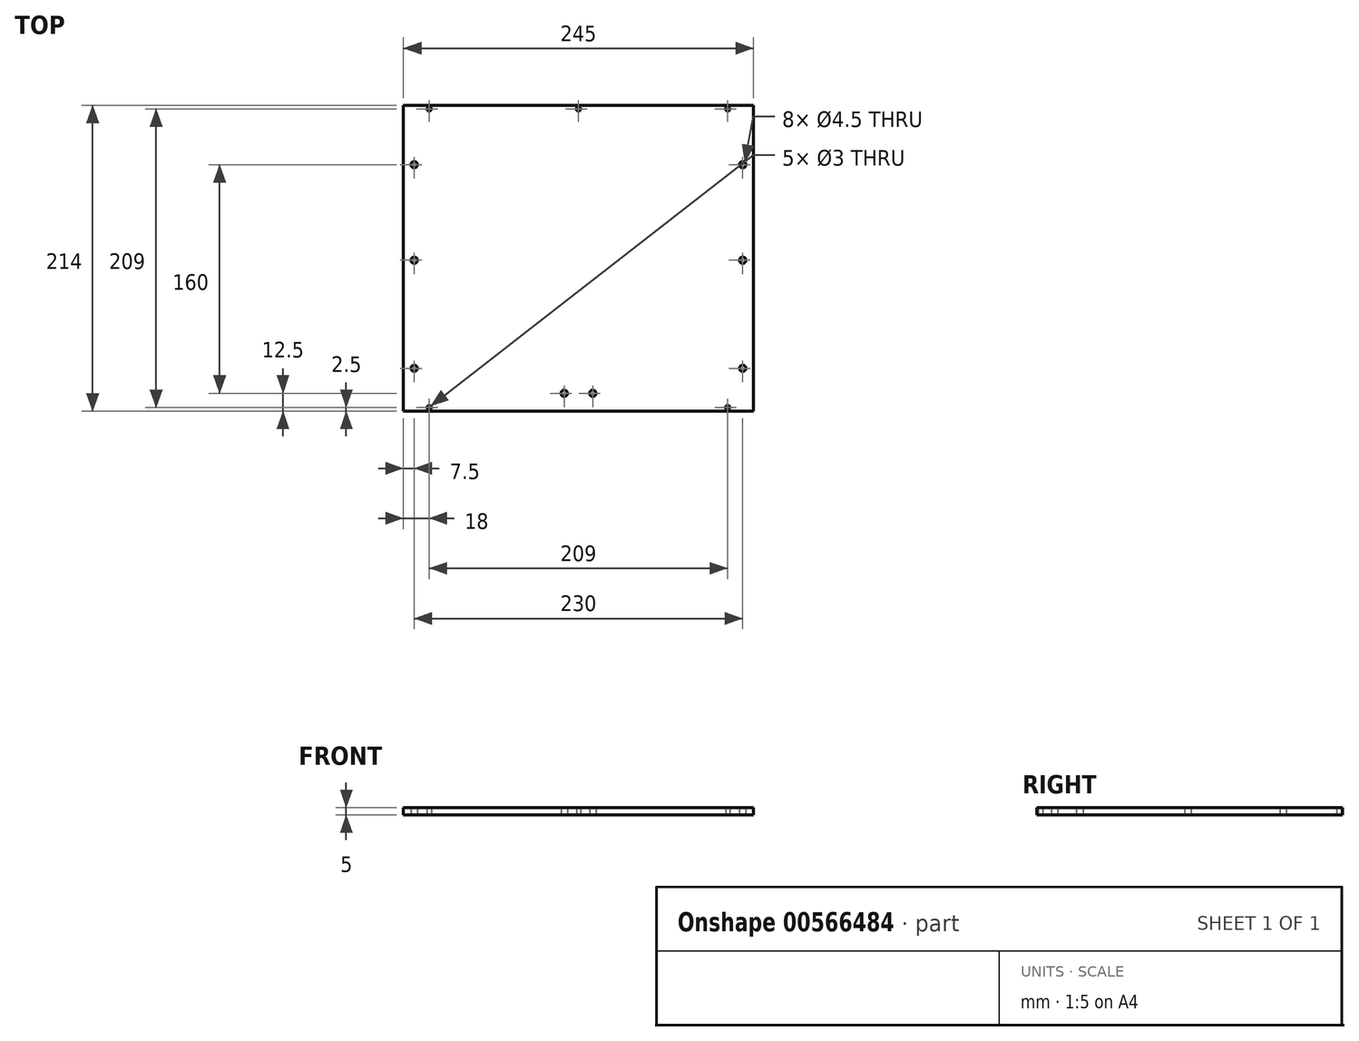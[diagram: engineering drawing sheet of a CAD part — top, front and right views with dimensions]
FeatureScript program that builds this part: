
annotation { "Feature Type Name" : "Feature", "Feature Type Description" : "" }
export const myFeature = defineFeature(function(context is Context, id is Id, definition is map)
    precondition{}
    {
        {
            var Q0;
            Q0=qCreatedBy(makeId("Top.planeOp"),FACE);
            var sketch = newSketch(context, id + "F0", { "sketchPlane" : qUnion([Q0])});
            skLineSegment(sketch, "E0.bottom", {"start": v(122.5, -107) * mm, "end": v(-122.5, -107) * mm});
            skLineSegment(sketch, "E0.top", {"start": v(122.5, 107) * mm, "end": v(-122.5, 107) * mm});
            skLineSegment(sketch, "E0.left", {"start": v(122.5, -107) * mm, "end": v(122.5, 0.95) * mm});
            skLineSegment(sketch, "E0.right", {"start": v(-122.5, -107) * mm, "end": v(-122.5, 0.95) * mm});
            skPoint(sketch, "E1.visualSharp", {"position": v(-122.5, 107) * mm});
            skLineSegment(sketch, "E1.filletArc", {"start": v(-122.5, 107) * mm, "end": v(-122.5, 107) * mm});
            skPoint(sketch, "E2.visualSharp", {"position": v(-122.5, -107) * mm});
            skLineSegment(sketch, "E2.filletArc", {"start": v(-122.5, -107) * mm, "end": v(-122.5, -107) * mm});
            skPoint(sketch, "E3.visualSharp", {"position": v(122.5, -107) * mm});
            skLineSegment(sketch, "E3.filletArc", {"start": v(122.5, -107) * mm, "end": v(122.5, -107) * mm});
            skPoint(sketch, "E4.visualSharp", {"position": v(122.5, 107) * mm});
            skLineSegment(sketch, "E4.filletArc", {"start": v(122.5, 107) * mm, "end": v(122.5, 107) * mm});
            skLineSegment(sketch, "E5.trimOffspring", {"start": v(-122.5, 0.95) * mm, "end": v(-122.5, 107) * mm});
            skLineSegment(sketch, "E6.trimOffspring", {"start": v(122.5, 0.95) * mm, "end": v(122.5, 107) * mm});
            skCircle(sketch, "E7", {"center": v(-104.5, 104.5) * mm, "radius": 1.5 * mm});
            skCircle(sketch, "E8", {"center": v(104.5, 104.5) * mm, "radius": 1.5 * mm});
            skCircle(sketch, "E9", {"center": v(-104.5, -104.5) * mm, "radius": 1.5 * mm});
            skCircle(sketch, "E10", {"center": v(104.5, -104.5) * mm, "radius": 1.5 * mm});
            skCircle(sketch, "E11", {"center": v(0, 104.5) * mm, "radius": 1.5 * mm});
            skLineSegment(sketch, "E12.bottom", {"start": v(104.5, -104.5) * mm, "end": v(-104.5, -104.5) * mm, "construction": true});
            skLineSegment(sketch, "E12.top", {"start": v(104.5, 104.5) * mm, "end": v(-104.5, 104.5) * mm, "construction": true});
            skLineSegment(sketch, "E12.left", {"start": v(104.5, -104.5) * mm, "end": v(104.5, 104.5) * mm, "construction": true});
            skLineSegment(sketch, "E12.right", {"start": v(-104.5, -104.5) * mm, "end": v(-104.5, 104.5) * mm, "construction": true});
            skCircle(sketch, "E13", {"center": v(-115, -77) * mm, "radius": 2.25 * mm});
            skCircle(sketch, "E14", {"center": v(-115, -1.38) * mm, "radius": 2.25 * mm});
            skCircle(sketch, "E15", {"center": v(-115, 65.5) * mm, "radius": 2.25 * mm});
            skCircle(sketch, "E16.MirrorC", {"center": v(115, -77) * mm, "radius": 2.25 * mm});
            skCircle(sketch, "E17.MirrorC", {"center": v(115, -1.38) * mm, "radius": 2.25 * mm});
            skCircle(sketch, "E18.MirrorC", {"center": v(115, 65.5) * mm, "radius": 2.25 * mm});
            skCircle(sketch, "E19", {"center": v(-10, -94.5) * mm, "radius": 2.25 * mm});
            skCircle(sketch, "E20.MirrorC", {"center": v(10, -94.5) * mm, "radius": 2.25 * mm});
            skSolve(sketch);
        }
        {
            var Q0;
            Q0=qSketchRegion(id+"F0",true);
            extrude(context, id + "F1", {"entities" : qUnion([Q0]), "endBound" : BoundingType.SYMMETRIC, "depth" : 5 * mm});
        }
    });
